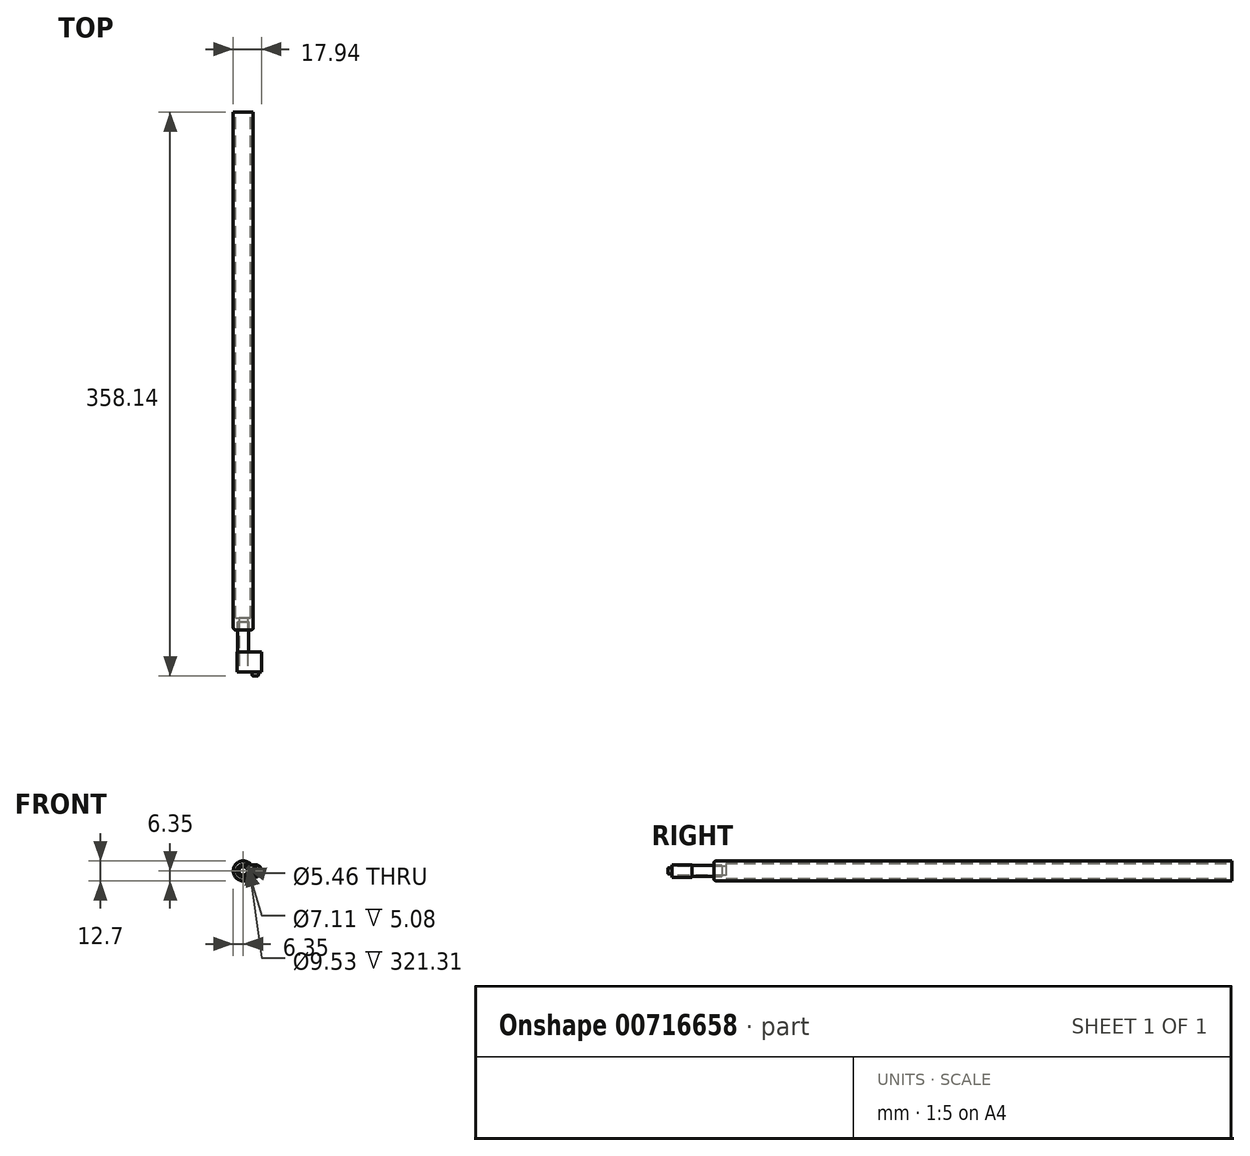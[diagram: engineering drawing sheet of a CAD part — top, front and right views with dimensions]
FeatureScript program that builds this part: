
annotation { "Feature Type Name" : "Feature", "Feature Type Description" : "" }
export const myFeature = defineFeature(function(context is Context, id is Id, definition is map)
    precondition{}
    {
        {
            var Q0;
            Q0=qCreatedBy(makeId("Front.planeOp"),FACE);
            var sketch = newSketch(context, id + "F0", { "sketchPlane" : qUnion([Q0])});
            skArc(sketch, "E0", {"start": v(0, 3.97) * mm, "mid": v(-3.97, 0) * mm, "end": v(0, -3.97) * mm});
            skArc(sketch, "E1", {"start": v(7.62, -3.97) * mm, "mid": v(11.59, 0) * mm, "end": v(7.62, 3.97) * mm});
            skLineSegment(sketch, "E2", {"start": v(0, 3.97) * mm, "end": v(7.62, 3.97) * mm});
            skLineSegment(sketch, "E3", {"start": v(0, -3.97) * mm, "end": v(7.62, -3.97) * mm});
            skCircle(sketch, "E4", {"center": v(0, 0) * mm, "radius": 2.73 * mm});
            skSolve(sketch);
        }
        {
            var Q0;
            Q0 = qSketchRegion(id + "F0", true);
            extrude(context, id + "F1", {"entities" : qUnion([Q0]), "oppositeDirection" : true, "depth" : 12.7 * mm, "offsetDistance" : 25.4 * mm});
        }
        {
            var Q0;
            Q0=makeQuery(id+"F1.opExtrude","CAP_FACE",FACE,{"disambiguationData":[OSD([sQuery(id+"F0.wireOp",EDGE,"E0"),sQuery(id+"F0.wireOp",EDGE,"E1"),sQuery(id+"F0.wireOp",EDGE,"E2"),sQuery(id+"F0.wireOp",EDGE,"E3"),sQuery(id+"F0.wireOp",EDGE,"E4")])],"isStart":false});
            var sketch = newSketch(context, id + "F2", { "sketchPlane" : qUnion([Q0])});
            skCircle(sketch, "E5", {"center": v(0, 0) * mm, "radius": 3.5 * mm});
            skSolve(sketch);
        }
        {
            var Q0;
            Q0 = qSketchRegion(id + "F2", true);
            extrude(context, id + "F3", {"entities" : qUnion([Q0]), "operationType" : NewBodyOperationType.REMOVE, "oppositeDirection" : true, "depth" : 6.35 * mm, "offsetDistance" : 25.4 * mm});
        }
        {
            var Q0;
            Q0=makeQuery(id+"F1.opExtrude","CAP_FACE",FACE,{"disambiguationData":[OSD([sQuery(id+"F0.wireOp",EDGE,"E0"),sQuery(id+"F0.wireOp",EDGE,"E1"),sQuery(id+"F0.wireOp",EDGE,"E2"),sQuery(id+"F0.wireOp",EDGE,"E3"),sQuery(id+"F0.wireOp",EDGE,"E4")])],"isStart":true});
            var sketch = newSketch(context, id + "F4", { "sketchPlane" : qUnion([Q0])});
            skCircle(sketch, "E6", {"center": v(7.62, 0) * mm, "radius": 1.98 * mm});
            skSolve(sketch);
        }
        {
            var Q0;
            Q0 = qSketchRegion(id + "F4", true);
            extrude(context, id + "F5", {"entities" : qUnion([Q0]), "operationType" : NewBodyOperationType.REMOVE, "oppositeDirection" : true, "depth" : 7.62 * mm, "offsetDistance" : 25.4 * mm});
        }
        {
            var Q0;
            Q0=makeQuery(id+"F3.boolean.opBoolean","COPY",FACE,{"derivedFrom":makeQuery(id+"F3.opExtrude","CAP_FACE",FACE,{"disambiguationData":[OSD([sQuery(id+"F2.wireOp",EDGE,"E5")])],"isStart":false})});
            var sketch = newSketch(context, id + "F6", { "sketchPlane" : qUnion([Q0])});
            skCircle(sketch, "E7", {"center": v(0, 0) * mm, "radius": 3.5 * mm});
            skCircle(sketch, "E8", {"center": v(0, 0) * mm, "radius": 2.73 * mm});
            skSolve(sketch);
        }
        {
            var Q0;
            Q0 = qSketchRegion(id + "F6", true);
            extrude(context, id + "F7", {"entities" : qUnion([Q0]), "operationType" : NewBodyOperationType.ADD, "depth" : 25.4 * mm, "offsetDistance" : 25.4 * mm});
        }
        {
            var Q0;
            Q0=makeQuery(id+"F5.boolean.opBoolean","COPY",FACE,{"derivedFrom":makeQuery(id+"F5.opExtrude","CAP_FACE",FACE,{"disambiguationData":[OSD([sQuery(id+"F4.wireOp",EDGE,"E6")])],"isStart":false})});
            var sketch = newSketch(context, id + "F8", { "sketchPlane" : qUnion([Q0])});
            skCircle(sketch, "E9", {"center": v(7.62, 0) * mm, "radius": 1.98 * mm});
            skSolve(sketch);
        }
        {
            var Q0;
            Q0 = qSketchRegion(id + "F8", true);
            extrude(context, id + "F9", {"entities" : qUnion([Q0]), "operationType" : NewBodyOperationType.ADD, "depth" : 10.16 * mm, "offsetDistance" : 25.4 * mm});
        }
        {
            var Q0;
            Q0=makeQuery(id+"F9.opExtrude","CAP_EDGE",EDGE,{"disambiguationData":[OSD([sQuery(id+"F8.wireOp",EDGE,"E9")])],"isStart":false});
            fillet(context, id + "F10", {"entities" : qUnion([Q0]), "radius" : 0.76 * mm, "tangentPropagation" : true, "allowEdgeOverflow" : false});
        }
        {
            var Q0;
            Q0=qCreatedBy(makeId("Right.planeOp"),FACE);
            var sketch = newSketch(context, id + "F11", { "sketchPlane" : qUnion([Q0])});
            skLineSegment(sketch, "E10", {"start": v(26.67, 3.56) * mm, "end": v(26.67, 4.76) * mm});
            skArc(sketch, "E11", {"start": v(26.67, 4.76) * mm, "mid": v(27.13, 5.89) * mm, "end": v(28.26, 6.35) * mm});
            skLineSegment(sketch, "E12", {"start": v(28.26, 6.35) * mm, "end": v(355.6, 6.35) * mm});
            skLineSegment(sketch, "E13", {"start": v(26.67, 3.56) * mm, "end": v(31.75, 3.56) * mm});
            skLineSegment(sketch, "E14", {"start": v(31.75, 3.56) * mm, "end": v(31.75, 2.73) * mm});
            skLineSegment(sketch, "E15", {"start": v(31.75, 2.73) * mm, "end": v(34.3, 2.73) * mm});
            skLineSegment(sketch, "E16", {"start": v(34.3, 2.73) * mm, "end": v(34.3, 4.76) * mm});
            skLineSegment(sketch, "E17", {"start": v(34.3, 4.76) * mm, "end": v(355.6, 4.76) * mm});
            skLineSegment(sketch, "E18", {"start": v(355.6, 6.35) * mm, "end": v(355.6, 4.76) * mm});
            skSolve(sketch);
        }
        {
            var Q0;
            Q0 = qSketchRegion(id + "F11", true);
            var Q1;
            Q1=makeQuery(id+"F7.opExtrude","SWEPT_FACE",FACE,{"disambiguationData":[OSD([sQuery(id+"F6.wireOp",EDGE,"E7")])]});
            revolve(context, id + "F12", {"operationType" : NewBodyOperationType.ADD, "surfaceOperationType" : NewSurfaceOperationType.NEW, "entities" : qUnion([Q0]), "axis" : qUnion([Q1]), "revolveType" : RevolveType.FULL});
        }
    });
